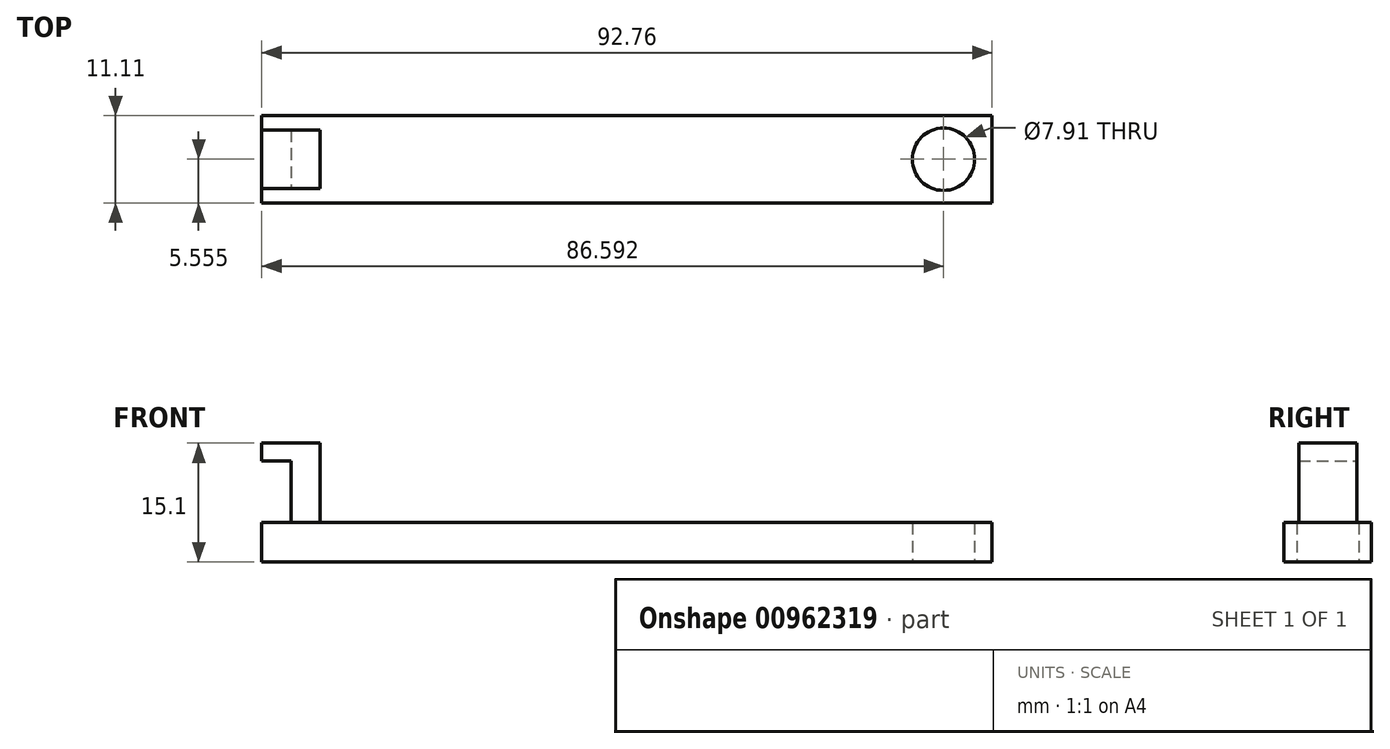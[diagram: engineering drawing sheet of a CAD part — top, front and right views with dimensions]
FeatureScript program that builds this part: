
annotation { "Feature Type Name" : "Feature", "Feature Type Description" : "" }
export const myFeature = defineFeature(function(context is Context, id is Id, definition is map)
    precondition{}
    {
        {
            var Q0;
            Q0=qCreatedBy(makeId("Top.planeOp"),FACE);
            var sketch = newSketch(context, id + "F0", { "sketchPlane" : qUnion([Q0])});
            skLineSegment(sketch, "E0.bottom", {"start": v(-47.4, 30.34) * mm, "end": v(45.35, 30.34) * mm});
            skLineSegment(sketch, "E0.top", {"start": v(-47.4, 19.23) * mm, "end": v(45.35, 19.23) * mm});
            skLineSegment(sketch, "E0.left", {"start": v(-47.4, 30.34) * mm, "end": v(-47.4, 19.23) * mm});
            skLineSegment(sketch, "E0.right", {"start": v(45.35, 30.34) * mm, "end": v(45.35, 19.23) * mm});
            skCircle(sketch, "E1", {"center": v(39.18, 24.78) * mm, "radius": 3.96 * mm});
            skPoint(sketch, "E1.centerSnap0", {"position": v(45.35, 24.78) * mm});
            skLineSegment(sketch, "E2.bottom", {"start": v(-36.3, 28.49) * mm, "end": v(-43.7, 28.49) * mm});
            skLineSegment(sketch, "E2.top", {"start": v(-36.3, 21.08) * mm, "end": v(-43.7, 21.08) * mm});
            skLineSegment(sketch, "E2.left", {"start": v(-36.3, 28.49) * mm, "end": v(-36.3, 21.08) * mm});
            skLineSegment(sketch, "E2.right", {"start": v(-43.7, 28.49) * mm, "end": v(-43.7, 21.08) * mm});
            skPoint(sketch, "E2.middle", {"position": v(-40, 24.78) * mm});
            skPoint(sketch, "E2.middle.positionSnap0", {"position": v(-47.4, 24.78) * mm});
            skPoint(sketch, "E2.centerSnap0", {"position": v(-47.4, 24.78) * mm});
            skLineSegment(sketch, "E3", {"start": v(-40, 28.49) * mm, "end": v(-40, 21.08) * mm});
            skSolve(sketch);
        }
        {
            var Q0;
            Q0 = qSketchRegion(id + "F0", true);
            var Q1;
            {var subQ0=sQuery(id+"F0.wireOp",EDGE,"E2.left");Q1=makeQuery(id+"F0.imprint","IMPRINT",FACE,{"disambiguationData":[TD([[makeQuery(id+"F0.imprint","IMPRINT",EDGE,{"derivedFrom":subQ0}),-1.0]])]});}
            extrude(context, id + "F1", {"entities" : qUnion([Q0, Q1]), "depth" : 5 * mm, "offsetDistance" : 25 * mm});
        }
        {
            var Q0;
            {var subQ0=sQuery(id+"F0.wireOp",EDGE,"E2.right");Q0=makeQuery(id+"F0.imprint","IMPRINT",FACE,{"disambiguationData":[TD([[makeQuery(id+"F0.imprint","IMPRINT",EDGE,{"derivedFrom":subQ0}),1.0]])]});}
            extrude(context, id + "F2", {"entities" : qUnion([Q0]), "operationType" : NewBodyOperationType.ADD, "depth" : 15.1 * mm, "offsetDistance" : 25 * mm});
        }
        {
            var Q0;
            Q0=makeQuery(id+"F2.opExtrude","SWEPT_FACE",FACE,{"disambiguationData":[OSD([sQuery(id+"F0.wireOp",EDGE,"E2.right")])]});
            var sketch = newSketch(context, id + "F3", { "sketchPlane" : qUnion([Q0])});
            skLineSegment(sketch, "E4.bottom", {"start": v(-21.08, 15.1) * mm, "end": v(-28.49, 15.1) * mm});
            skLineSegment(sketch, "E4.top", {"start": v(-21.08, 12.86) * mm, "end": v(-28.49, 12.86) * mm});
            skLineSegment(sketch, "E4.left", {"start": v(-21.08, 15.1) * mm, "end": v(-21.08, 12.86) * mm});
            skLineSegment(sketch, "E4.right", {"start": v(-28.49, 15.1) * mm, "end": v(-28.49, 12.86) * mm});
            skSolve(sketch);
        }
        {
            var Q0;
            Q0 = qSketchRegion(id + "F3", true);
            var Q1;
            Q1=makeQuery(id+"F1.opExtrude","SWEPT_FACE",FACE,{"disambiguationData":[OSD([sQuery(id+"F0.wireOp",EDGE,"E0.left")])]});
            extrude(context, id + "F4", {"entities" : qUnion([Q0]), "operationType" : NewBodyOperationType.ADD, "endBound" : BoundingType.UP_TO_SURFACE, "depth" : 25 * mm, "endBoundEntityFace" : qUnion([Q1]), "offsetDistance" : 25 * mm});
        }
    });
